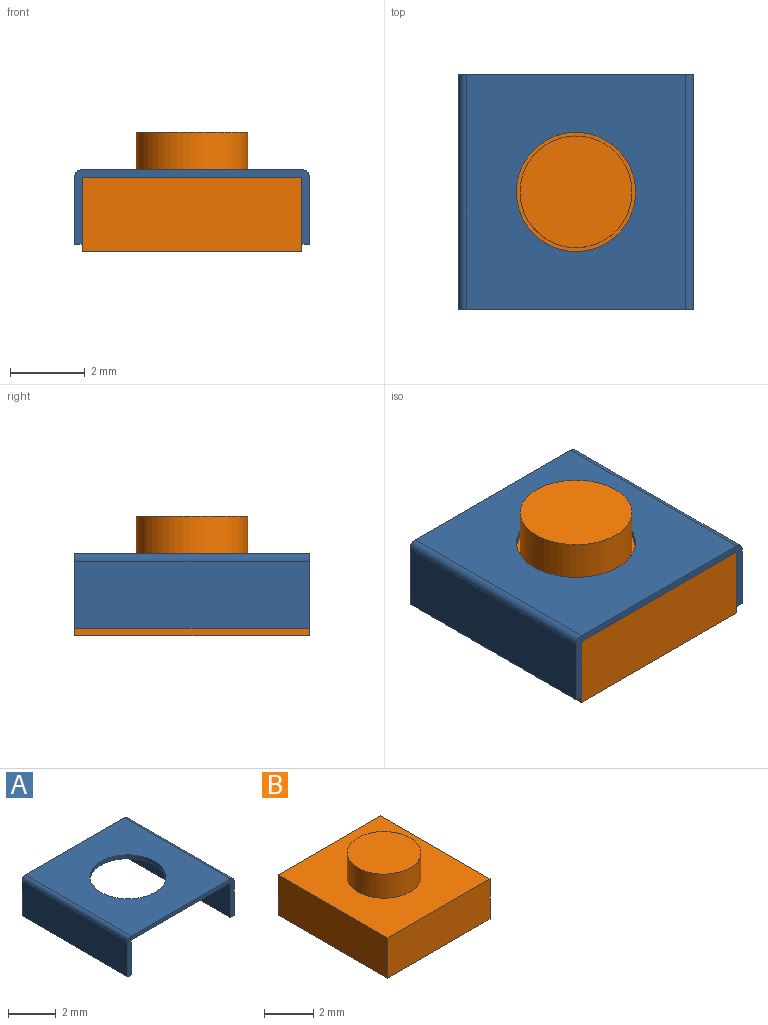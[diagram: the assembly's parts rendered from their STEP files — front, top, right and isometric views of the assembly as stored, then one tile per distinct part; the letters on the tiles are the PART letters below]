
ASSEMBLY  parts=2 mates=1
PART A: 13 faces, bbox 6.3x6.3x2 mm
  f0: plane 6.3x5.9mm, normal (0,0,-1), area 29.1mm2, adj f1,f3,f4,f7,f9
  f1: plane 6.3x2mm, normal (0,1,0), area 2mm2, adj f0,f2,f5,f6,f7,f8,f9,f10
  f2: plane 6.3x1.8mm, normal (-1,0,0), area 11.3mm2, adj f1,f3,f8,f11
  f3: plane 6.3x2mm, normal (0,-1,0), area 2mm2, adj f0,f2,f5,f6,f7,f8,f9,f10
  f4: cylinder r=1.6mm len=3.2mm, axis (0,0,-1), area 2mm2, adj f0,f6
  f5: plane 6.3x1.8mm, normal (1,0,0), area 11.3mm2, adj f1,f3,f10,f12
  f6: plane 6.3x5.9mm, normal (0,0,1), area 29.1mm2, adj f1,f3,f4,f11,f12
  f7: plane 6.3x1.8mm, normal (1,0,0), area 11.3mm2, adj f0,f1,f3,f8
  f8: plane 6.3x0.2mm, normal (0,0,-1), area 1.3mm2, adj f1,f2,f3,f7
  f9: plane 6.3x1.8mm, normal (-1,0,0), area 11.3mm2, adj f0,f1,f3,f10
  f10: plane 6.3x0.2mm, normal (0,0,-1), area 1.3mm2, adj f1,f3,f5,f9
  f11: cylinder r=0.2mm len=6.3mm, axis (0,1,0), area 2mm2, adj f1,f2,f3,f6
  f12: cylinder r=0.2mm len=6.3mm, axis (0,-1,0), area 2mm2, adj f1,f3,f5,f6
PART B: 8 faces, bbox 5.9x6.3x3.2 mm
  f0: plane 5.9x2mm, normal (0,1,0), area 11.8mm2, adj f1,f3,f4,f5
  f1: plane 6.3x2mm, normal (-1,0,0), area 12.6mm2, adj f0,f2,f4,f5
  f2: plane 5.9x2mm, normal (0,-1,0), area 11.8mm2, adj f1,f3,f4,f5
  f3: plane 6.3x2mm, normal (1,0,0), area 12.6mm2, adj f0,f2,f4,f5
  f4: plane 6.3x5.9mm, normal (0,0,1), area 30.1mm2, adj f0,f1,f2,f3,f6
  f5: plane 6.3x5.9mm, normal (0,0,-1), area 37.2mm2, adj f0,f1,f2,f3
  f6: cylinder r=1.5mm len=3mm, axis (0,0,-1), area 11.3mm2, adj f4,f7
  f7: plane 3x3mm, normal (0,0,1), area 7.1mm2, adj f6
PLACE A t=(-2.39,0.18,5.13)mm
PLACE B t=(-2.19,0.18,3.13)mm
MATE fastened B.f6 <-> A.f4  axis (0,0,-1) through (0.76,3.33,5.13)mm
